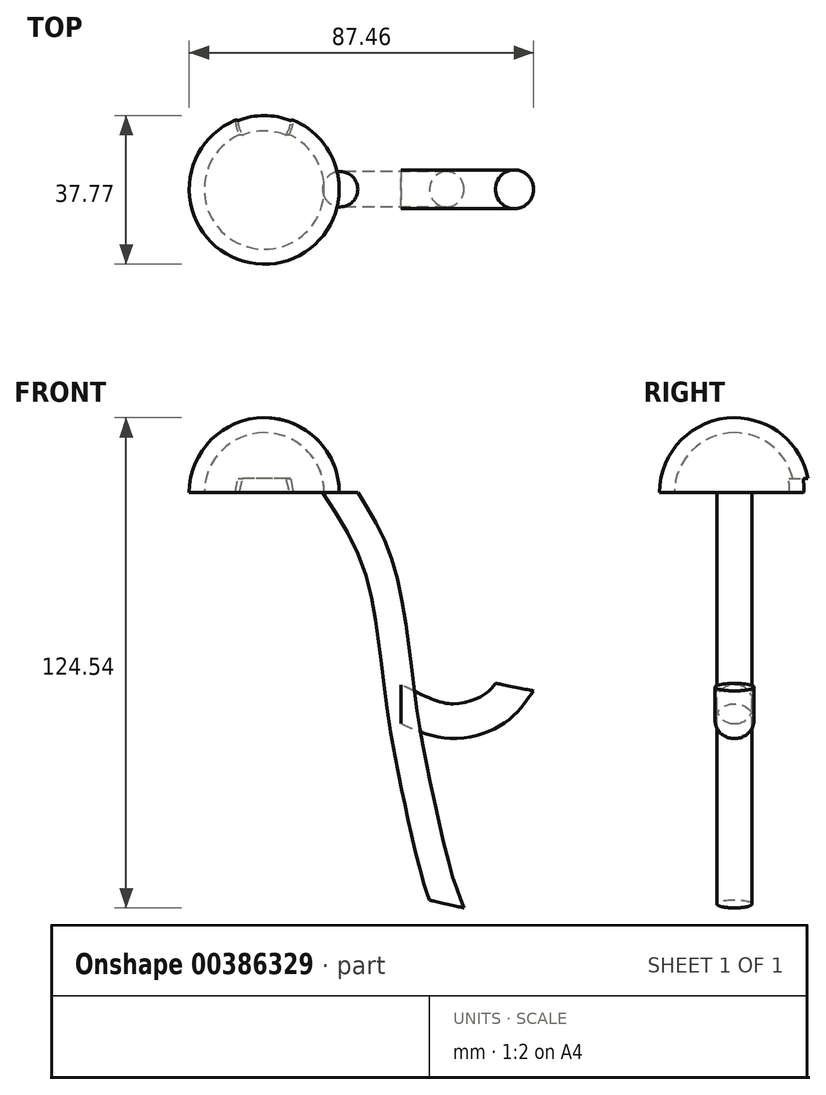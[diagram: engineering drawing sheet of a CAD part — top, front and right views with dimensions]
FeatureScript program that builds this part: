
annotation { "Feature Type Name" : "Feature", "Feature Type Description" : "" }
export const myFeature = defineFeature(function(context is Context, id is Id, definition is map)
    precondition{}
    {
        {
            var Q0;
            Q0=qCreatedBy(makeId("Front.planeOp"),FACE);
            var sketch = newSketch(context, id + "F0", { "sketchPlane" : qUnion([Q0])});
            skArc(sketch, "E0", {"start": v(0, -19.05) * mm, "mid": v(19.05, 0) * mm, "end": v(0, 19.05) * mm});
            skLineSegment(sketch, "E1", {"start": v(0, 19.05) * mm, "end": v(0, -19.05) * mm});
            skSolve(sketch);
        }
        {
            var Q0;
            Q0=qCreatedBy(makeId("Front.planeOp"),FACE);
            var sketch = newSketch(context, id + "F1", { "sketchPlane" : qUnion([Q0])});
            skLineSegment(sketch, "E2", {"start": v(0, 68.95) * mm, "end": v(0, -51.54) * mm, "construction": true});
            skSolve(sketch);
        }
        {
            var Q0;
            Q0 = qSketchRegion(id + "F0", true);
            var Q1;
            Q1=sQuery(id+"F1.wireOp",EDGE,"E2");
            revolve(context, id + "F2", {"entities" : qUnion([Q0]), "axis" : qUnion([Q1]), "revolveType" : RevolveType.FULL});
        }
        {
            var Q0;
            Q0=qCreatedBy(makeId("Top.planeOp"),FACE);
            var sketch = newSketch(context, id + "F3", { "sketchPlane" : qUnion([Q0])});
            skLineSegment(sketch, "E3.bottom", {"start": v(-20, 20.47) * mm, "end": v(20, 20.47) * mm});
            skLineSegment(sketch, "E3.top", {"start": v(-20, -20.7) * mm, "end": v(20, -20.7) * mm});
            skLineSegment(sketch, "E3.left", {"start": v(-20, 20.47) * mm, "end": v(-20, -20.7) * mm});
            skLineSegment(sketch, "E3.right", {"start": v(20, 20.47) * mm, "end": v(20, -20.7) * mm});
            skSolve(sketch);
        }
        {
            var Q0;
            Q0=makeQuery(id+"F3.imprint","IMPRINT",FACE,{"disambiguationData":[TD([[makeQuery(id+"F3.imprint","IMPRINT",EDGE,{"derivedFrom":sQuery(id+"F3.wireOp",EDGE,"E3.bottom")}),-1.0]])]});
            extrude(context, id + "F4", {"entities" : qUnion([Q0]), "operationType" : NewBodyOperationType.REMOVE, "oppositeDirection" : true, "depth" : 19.8 * mm});
        }
        {
            var Q0;
            Q0=makeQuery(id+"F4.boolean.opBoolean","COPY",FACE,{"derivedFrom":makeQuery(id+"F4.opExtrude","CAP_FACE",FACE,{"disambiguationData":[OSD([sQuery(id+"F3.wireOp",EDGE,"E3.bottom"),sQuery(id+"F3.wireOp",EDGE,"E3.top"),sQuery(id+"F3.wireOp",EDGE,"E3.left"),sQuery(id+"F3.wireOp",EDGE,"E3.right")])],"isStart":true})});
            shell(context, id + "F5", {"entities" : qUnion([Q0]), "thickness" : 3.8 * mm});
        }
        {
            var Q0;
            Q0=qCreatedBy(makeId("Top.planeOp"),FACE);
            var sketch = newSketch(context, id + "F6", { "sketchPlane" : qUnion([Q0])});
            skCircle(sketch, "E4", {"center": v(19.3, 0) * mm, "radius": 4.48 * mm});
            skSolve(sketch);
        }
        {
            var Q0;
            Q0=qCreatedBy(makeId("Front.planeOp"),FACE);
            var sketch = newSketch(context, id + "F7", { "sketchPlane" : qUnion([Q0])});
            skFitSpline(sketch, "E5", {"points": [v(19.37, 0) * mm, v(29.05, -18.7) * mm, v(34.4, -50.1) * mm, v(38.07, -71.8) * mm, v(43.75, -96.51) * mm, v(46.42, -104.53) * mm], "startDerivative": vector(54.3, -82.96) * mm, "endDerivative": vector(19.68, -52.42) * mm});
            skSolve(sketch);
        }
        {
            var Q0;
            Q0=makeQuery(id+"F6.imprint","IMPRINT",FACE,{"disambiguationData":[TD([[makeQuery(id+"F6.imprint","IMPRINT",EDGE,{"derivedFrom":sQuery(id+"F6.wireOp",EDGE,"E4")}),1.0]])]});
            var Q1;
            Q1=sQuery(id+"F7.wireOp",EDGE,"E5");
            sweep(context, id + "F8", {"operationType" : NewBodyOperationType.ADD, "profiles" : qUnion([Q0]), "path" : qUnion([Q1])});
        }
        {
            var Q0;
            Q0=qCreatedBy(makeId("Top.planeOp"),FACE);
            var sketch = newSketch(context, id + "F9", { "sketchPlane" : qUnion([Q0])});
            skCircle(sketch, "E6", {"center": v(0, 17.73) * mm, "radius": 7.36 * mm});
            skSolve(sketch);
        }
        {
            var Q0;
            Q0=makeQuery(id+"F9.imprint","IMPRINT",FACE,{"disambiguationData":[TD([[makeQuery(id+"F9.imprint","IMPRINT",EDGE,{"derivedFrom":sQuery(id+"F9.wireOp",EDGE,"E6")}),1.0]])]});
            extrude(context, id + "F10", {"entities" : qUnion([Q0]), "operationType" : NewBodyOperationType.REMOVE, "depth" : 3.56 * mm, "hasDraft" : true, "draftAngle" : 10 * degree, "draftPullDirection" : true});
        }
        {
            var Q0;
            Q0=qCreatedBy(makeId("Front.planeOp"),FACE);
            var sketch = newSketch(context, id + "F11", { "sketchPlane" : qUnion([Q0])});
            skFitSpline(sketch, "E7", {"points": [v(35.4, -52.59) * mm, v(47.84, -56.62) * mm, v(57.98, -53.46) * mm, v(62.57, -48.57) * mm], "startDerivative": vector(32.46, -15.41) * mm, "endDerivative": vector(13.95, 18.81) * mm});
            skSolve(sketch);
        }
        {
            var Q0;
            Q0=qCreatedBy(makeId("Right.planeOp"),FACE);
            cPlane(context, id + "F12", {"entities" : qUnion([Q0]), "cplaneType" : CPlaneType.OFFSET, "offset" : 34.8 * mm, "width" : 152.4 * mm, "height" : 152.4 * mm});
        }
        {
            var Q0;
            Q0=qCreatedBy(id+"F12.planeOp",FACE);
            var sketch = newSketch(context, id + "F13", { "sketchPlane" : qUnion([Q0])});
            skCircle(sketch, "E8", {"center": v(0, -53.73) * mm, "radius": 4.93 * mm});
            skSolve(sketch);
        }
        {
            var Q0;
            Q0 = qSketchRegion(id + "F13", true);
            var Q1;
            Q1=sQuery(id+"F11.wireOp",EDGE,"E7");
            sweep(context, id + "F14", {"profiles" : qUnion([Q0]), "path" : qUnion([Q1])});
        }
    });
